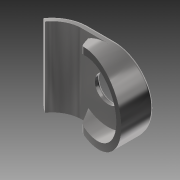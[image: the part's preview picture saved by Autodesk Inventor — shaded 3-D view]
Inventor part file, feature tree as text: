
AUTODESK INVENTOR PART (.ipt)
format: ipt  version: 2013 (Build 170138000, 138)  size: 221,184 bytes
history: native  units: mm
features: sketch x5, other x3, fillet x3, extrude x2, revolve x1, plane x1
ambient origin geometry x8: Origin, YZ Plane, XZ Plane, XY Plane, X Axis, Y Axis, Z Axis, Center Point
feature tree (15):
  other  "Sólido1"
  sketch  "Boceto1"  dims[d63=2.0mm d64=10.0mm]
  revolve  "Revolución3"  [1 undecoded]
  sketch  "Boceto5"  dims[d65=6.0mm d66=0.2mm]
  extrude  "Extrusión4"  Depth=0.2mm
  extrude  "Extrusión5"  Depth=1.8mm
  other  "Suprimir cara4"
  other  "Suprimir cara5"
  fillet  "Empalme8"  Radius=6.0mm
  fillet  "Empalme9"  Radius=8.0mm
  fillet  "Empalme10"  [1 undecoded]
  sketch  "Boceto7"  dims[d72=4.0mm]
  sketch  "Boceto8"  dims[d97=1.0mm d98=4.0mm d99=2.0mm d100=14.0mm d101=10.0mm d103=0.0mm d104=0.0mm d106=180.0deg d107=2.0mm d108=4.0mm d110=2.0mm d111=9.0mm d112=22.0mm d114=2.0mm d115=24.0mm d116=0.0mm d117=1.0mm d118=2.0mm d119=1.0mm d120=2.0mm]
  plane  "Plano de trabajo2"
  sketch  "Boceto6"  dims[d67=2.0mm d68=1.8mm d69=6.0mm d70=8.0mm d71=90.0deg]
note: 2 required parameter values undecoded (feature->parameter linkage not recoverable at this tier; creation-order binding heuristic only, values carry confidence <= 0.55)